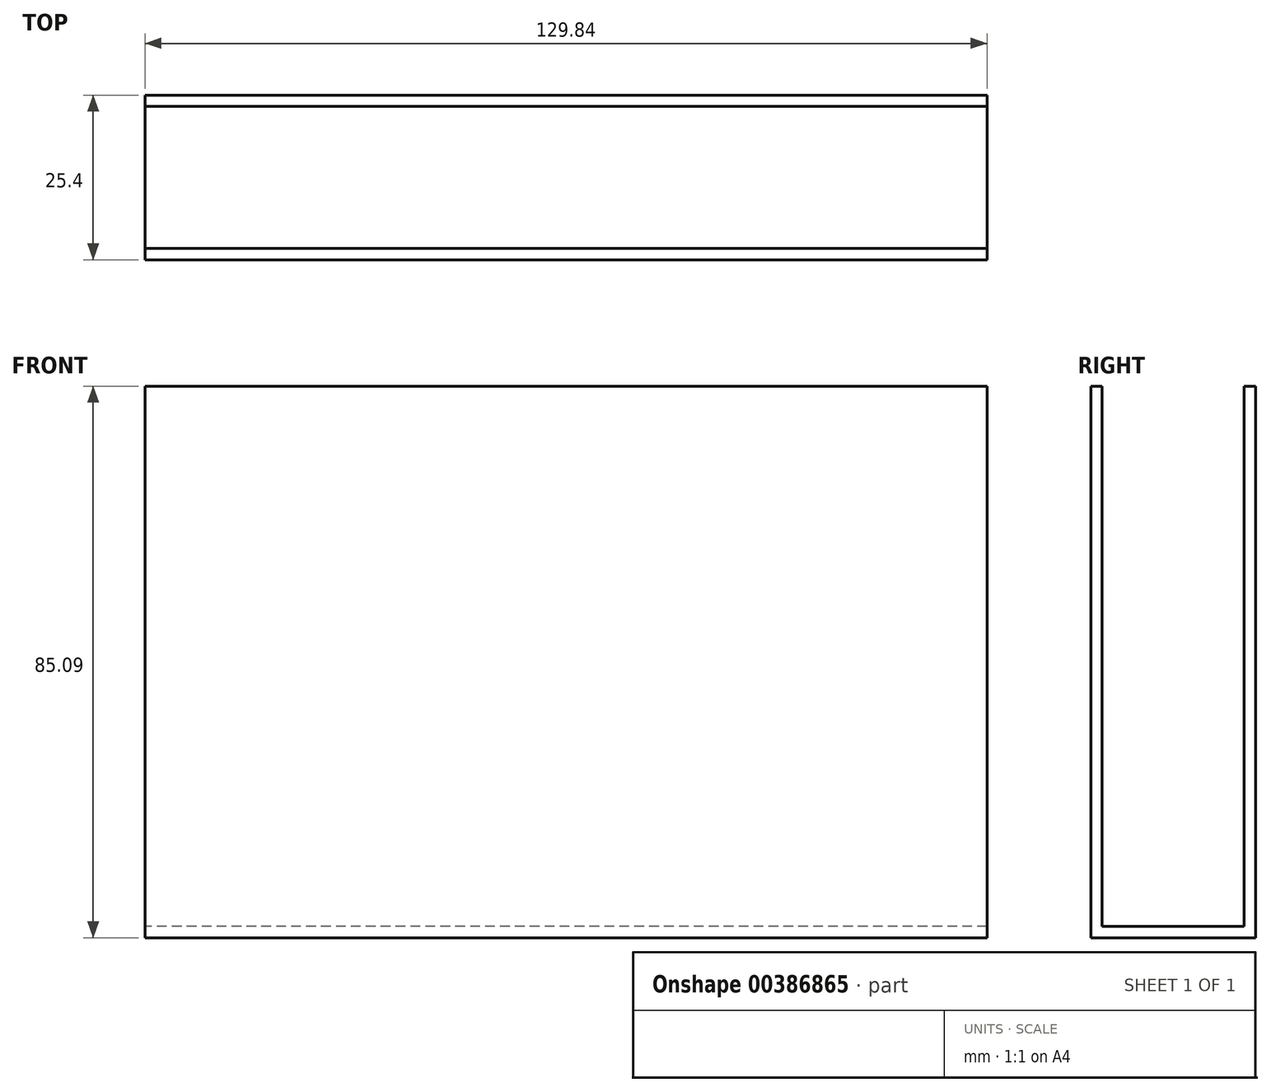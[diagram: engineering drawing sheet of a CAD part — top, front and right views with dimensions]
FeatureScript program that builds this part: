
annotation { "Feature Type Name" : "Feature", "Feature Type Description" : "" }
export const myFeature = defineFeature(function(context is Context, id is Id, definition is map)
    precondition{}
    {
        {
            var Q0;
            Q0=qCreatedBy(makeId("Top.planeOp"),FACE);
            var sketch = newSketch(context, id + "F0", { "sketchPlane" : qUnion([Q0])});
            skLineSegment(sketch, "E0.bottom", {"start": v(66.68, 12.7) * mm, "end": v(-66.68, 12.7) * mm});
            skLineSegment(sketch, "E0.top", {"start": v(66.68, -12.7) * mm, "end": v(-66.68, -12.7) * mm});
            skLineSegment(sketch, "E0.left", {"start": v(66.68, 12.7) * mm, "end": v(66.68, -12.7) * mm});
            skLineSegment(sketch, "E0.right", {"start": v(-66.68, 12.7) * mm, "end": v(-66.68, -12.7) * mm});
            skPoint(sketch, "E0.middle", {"position": v(0, 0) * mm});
            skSolve(sketch);
        }
        {
            var Q0;
            Q0 = qSketchRegion(id + "F0", true);
            extrude(context, id + "F1", {"entities" : qUnion([Q0]), "depth" : 85.1 * mm});
        }
        {
            var Q0;
            Q0=makeQuery(id+"F1.opExtrude","CAP_FACE",FACE,{"disambiguationData":[OSD([sQuery(id+"F0.wireOp",EDGE,"E0.bottom"),sQuery(id+"F0.wireOp",EDGE,"E0.top"),sQuery(id+"F0.wireOp",EDGE,"E0.left"),sQuery(id+"F0.wireOp",EDGE,"E0.right")])],"isStart":false});
            shell(context, id + "F2", {"entities" : qUnion([Q0]), "thickness" : 1.75 * mm});
        }
        {
            var Q0;
            Q0=makeQuery(id+"F1.opExtrude","SWEPT_FACE",FACE,{"disambiguationData":[OSD([sQuery(id+"F0.wireOp",EDGE,"E0.right")])]});
            extrude(context, id + "F3", {"entities" : qUnion([Q0]), "operationType" : NewBodyOperationType.REMOVE, "oppositeDirection" : true, "depth" : 1.75 * mm});
        }
        {
            var Q0;
            Q0=makeQuery(id+"F1.opExtrude","SWEPT_FACE",FACE,{"disambiguationData":[OSD([sQuery(id+"F0.wireOp",EDGE,"E0.left")])]});
            extrude(context, id + "F4", {"entities" : qUnion([Q0]), "operationType" : NewBodyOperationType.REMOVE, "oppositeDirection" : true, "depth" : 1.75 * mm});
        }
    });
